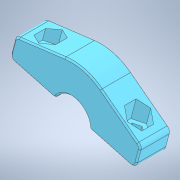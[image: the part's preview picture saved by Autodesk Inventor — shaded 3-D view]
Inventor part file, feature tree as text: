
AUTODESK INVENTOR PART (.ipt)
format: ipt  version: 2021.2 (Build 252289000, 289)  size: 267,264 bytes
history: native  units: mm
features: other x4, fillet x1, chamfer x1
ambient origin geometry x8: Origin, YZ Plane, XZ Plane, XY Plane, X Axis, Y Axis, Z Axis, Center Point
bodies: Body1 (feature_tree)
feature tree (6):
  other  "Твёрдое тело.ipt"
  fillet  "Сопряжение1"  Radius=10.0mm
  chamfer  "Фаска1"  Distance=2.0mm
  other  "Скобка 2::Твёрдое тело.ipt"
  other  "Элемент создания тегов1"
  other  "Твердое тело1"
